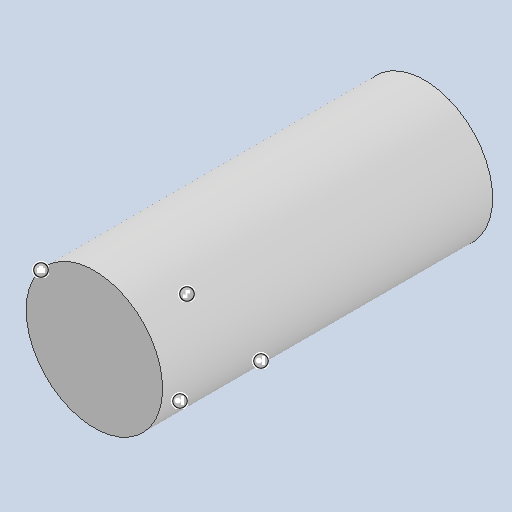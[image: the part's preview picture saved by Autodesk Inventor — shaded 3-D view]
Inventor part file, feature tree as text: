
AUTODESK INVENTOR PART (.ipt)
format: ipt  version: 2024.3 (Build 283343000, 343)  size: 205,824 bytes
history: native  units: mm
features: extrude x1
ambient origin geometry x8: Origin, YZ Plane, XZ Plane, XY Plane, X Axis, Y Axis, Z Axis, Center Point
bodies: Solid1 (feature_tree)
feature tree (1):
  extrude  "Extrusion1"  TaperAngle=0.0deg  [1 undecoded]
note: 1 required parameter value undecoded (feature->parameter linkage not recoverable at this tier; creation-order binding heuristic only, values carry confidence <= 0.55)
